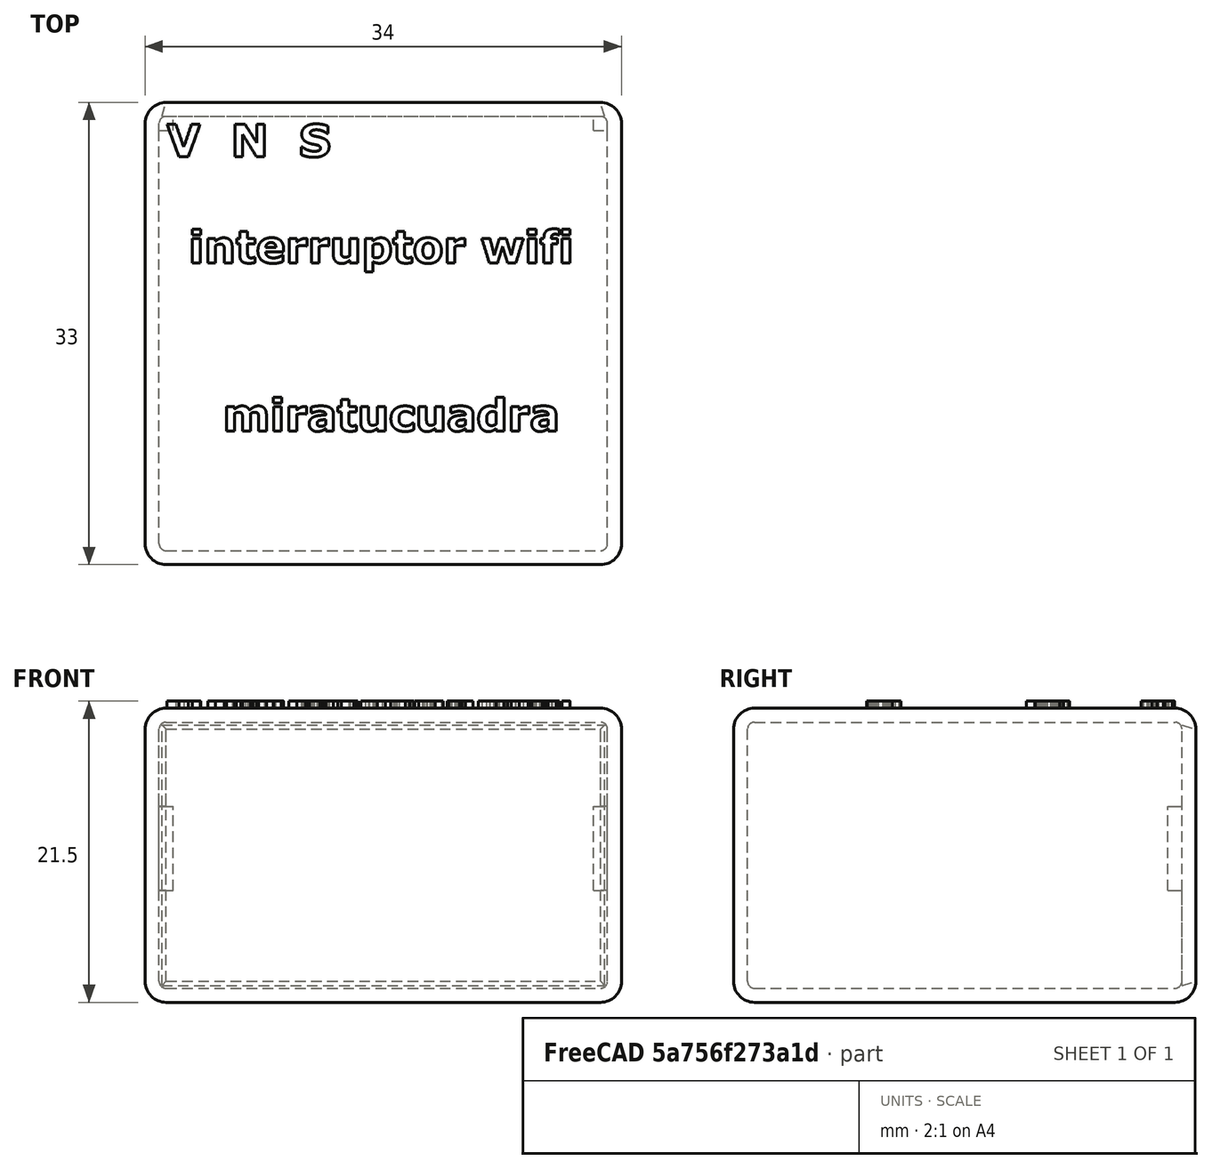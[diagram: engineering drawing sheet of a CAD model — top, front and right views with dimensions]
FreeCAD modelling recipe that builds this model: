
FCSTD DOCUMENT  (FreeCAD 0.20R29410 (Git))
Label: device01_carcaza sola
License: All rights reserved
LicenseURL: http://en.wikipedia.org/wiki/All_rights_reserved
objects: Part::Extrusion×65, Part::Feature×41, Part::Cut×10, Part::Box×5, Part::MultiFuse×5, Part::Fillet×2, Part::Wedge×1
note: 129 computed .brp shape members not serialized (recipe doc carries the construction recipe); baked Part::Feature solids carry a one-line shape summary decoded from their .brp

FEATURE [Part::Box] Box010  label="fundaprisma"
  AttacherType = Attacher::AttachEngine3D
  Height = 21
  Length = 34
  Placement = pos=(-1.3,-7.5,-3) rot=(0,0,1;0rad)
  Width = 33
FEATURE [Part::Feature] path3990
  shape: bbox 2.35 x 2.308 x 2e-07 mm, 0 faces, 0 solids (baked)
FEATURE [Part::Extrusion] Extrude
  Base = -> path3990
  Dir = (0,0,-1)
  DirMode = 2
  FaceMakerClass = Part::FaceMakerBullseye
  LengthFwd = 1
  LengthRev = 0
  Solid = true
  Symmetric = false
FEATURE [Part::Feature] path3992
  shape: bbox 2.099 x 2.308 x 2e-07 mm, 0 faces, 0 solids (baked)
FEATURE [Part::Extrusion] Extrude001
  Base = -> path3992
  Dir = (0,0,-1)
  DirMode = 2
  FaceMakerClass = Part::FaceMakerBullseye
  LengthFwd = 1
  LengthRev = 0
  Solid = true
  Symmetric = false
FEATURE [Part::Feature] path3994
  shape: bbox 1.974 x 2.392 x 2e-07 mm, 0 faces, 0 solids (baked)
FEATURE [Part::Extrusion] Extrude002
  Base = -> path3994
  Dir = (0,0,-1)
  DirMode = 2
  FaceMakerClass = Part::FaceMakerBullseye
  LengthFwd = 1
  LengthRev = 0
  Solid = true
  Symmetric = false
FEATURE [Part::MultiFuse] Fusion003  label="v n s"
  Placement = pos=(6,23,18.5) rot=(0,0,1;0rad)
  Shapes = -> [Extrude002,Extrude,Extrude001]
FEATURE [Part::Feature] path3995
  shape: bbox 0.5581 x 1.741 x 2e-07 mm, 0 faces, 0 solids (baked)
FEATURE [Part::Extrusion] Extrude003
  Base = -> path3995
  Dir = (0,0,-1)
  DirMode = 2
  FaceMakerClass = Part::FaceMakerBullseye
  LengthFwd = 1
  LengthRev = 0
  Solid = true
  Symmetric = false
FEATURE [Part::Extrusion] Extrude022
  Base = -> path3995
  Dir = (0,0,-1)
  DirMode = 2
  FaceMakerClass = Part::FaceMakerBullseye
  LengthFwd = 1
  LengthRev = 0
  Solid = true
  Symmetric = false
FEATURE [Part::Feature] path3990001
  shape: bbox 0.5891 x 0.4232 x 2e-07 mm, 0 faces, 0 solids (baked)
FEATURE [Part::Extrusion] Extrude004
  Base = -> path3990001
  Dir = (0,0,-1)
  DirMode = 2
  FaceMakerClass = Part::FaceMakerBullseye
  LengthFwd = 1
  LengthRev = 0
  Solid = true
  Symmetric = false
FEATURE [Part::Extrusion] Extrude023
  Base = -> path3990001
  Dir = (0,0,-1)
  DirMode = 2
  FaceMakerClass = Part::FaceMakerBullseye
  LengthFwd = 1
  LengthRev = 0
  Solid = true
  Symmetric = false
FEATURE [Part::Feature] path3990002
  shape: bbox 1.749 x 1.789 x 2e-07 mm, 0 faces, 0 solids (baked)
FEATURE [Part::Extrusion] Extrude005
  Base = -> path3990002
  Dir = (0,0,-1)
  DirMode = 2
  FaceMakerClass = Part::FaceMakerBullseye
  LengthFwd = 1
  LengthRev = 0
  Solid = true
  Symmetric = false
FEATURE [Part::Extrusion] Extrude024
  Base = -> path3990002
  Dir = (0,0,-1)
  DirMode = 2
  FaceMakerClass = Part::FaceMakerBullseye
  LengthFwd = 1
  LengthRev = 0
  Solid = true
  Symmetric = false
FEATURE [Part::Feature] path3990003
  shape: bbox 1.31 x 2.273 x 2e-07 mm, 0 faces, 0 solids (baked)
FEATURE [Part::Extrusion] Extrude006
  Base = -> path3990003
  Dir = (0,0,-1)
  DirMode = 2
  FaceMakerClass = Part::FaceMakerBullseye
  LengthFwd = 1
  LengthRev = 0
  Solid = true
  Symmetric = false
FEATURE [Part::Extrusion] Extrude025
  Base = -> path3990003
  Dir = (0,0,-1)
  DirMode = 2
  FaceMakerClass = Part::FaceMakerBullseye
  LengthFwd = 1
  LengthRev = 0
  Solid = true
  Symmetric = false
FEATURE [Part::Feature] path3996
  shape: bbox 1.842 x 1.842 x 2e-07 mm, 0 faces, 0 solids (baked)
FEATURE [Part::Extrusion] Extrude007
  Base = -> path3996
  Dir = (0,0,-1)
  DirMode = 2
  FaceMakerClass = Part::FaceMakerBullseye
  LengthFwd = 1
  LengthRev = 0
  Solid = true
  Symmetric = false
FEATURE [Part::Feature] path3996001
  shape: bbox 0.724 x 0.3519 x 2e-07 mm, 0 faces, 0 solids (baked)
FEATURE [Part::Extrusion] Extrude008
  Base = -> path3996001
  Dir = (0,0,1)
  DirMode = 2
  FaceMakerClass = Part::FaceMakerBullseye
  LengthFwd = 1
  LengthRev = 0
  Placement = pos=(0,0,-1) rot=(0,0,1;0rad)
  Solid = true
  Symmetric = false
FEATURE [Part::Cut] Cut003
  Base = -> Extrude007
  Tool = -> Extrude008
FEATURE [Part::Feature] path3998
  shape: bbox 1.262 x 1.747 x 2e-07 mm, 0 faces, 0 solids (baked)
FEATURE [Part::Extrusion] Extrude009
  Base = -> path3998
  Dir = (0,0,-1)
  DirMode = 2
  FaceMakerClass = Part::FaceMakerBullseye
  LengthFwd = 1
  LengthRev = 0
  Solid = true
  Symmetric = false
FEATURE [Part::Extrusion] Extrude027
  Base = -> path3998
  Dir = (0,0,-1)
  DirMode = 2
  FaceMakerClass = Part::FaceMakerBullseye
  LengthFwd = 1
  LengthRev = 0
  Solid = true
  Symmetric = false
FEATURE [Part::Feature] path4000
  shape: bbox 1.262 x 1.747 x 2e-07 mm, 0 faces, 0 solids (baked)
FEATURE [Part::Extrusion] Extrude010
  Base = -> path4000
  Dir = (0,0,-1)
  DirMode = 2
  FaceMakerClass = Part::FaceMakerBullseye
  LengthFwd = 1
  LengthRev = 0
  Solid = true
  Symmetric = false
FEATURE [Part::Extrusion] Extrude028
  Base = -> path4000
  Dir = (0,0,-1)
  DirMode = 2
  FaceMakerClass = Part::FaceMakerBullseye
  LengthFwd = 1
  LengthRev = 0
  Solid = true
  Symmetric = false
FEATURE [Part::Feature] path4002
  shape: bbox 1.749 x 1.789 x 2e-07 mm, 0 faces, 0 solids (baked)
FEATURE [Part::Extrusion] Extrude011
  Base = -> path4002
  Dir = (0,0,-1)
  DirMode = 2
  FaceMakerClass = Part::FaceMakerBullseye
  LengthFwd = 1
  LengthRev = 0
  Solid = true
  Symmetric = false
FEATURE [Part::Extrusion] Extrude029
  Base = -> path4002
  Dir = (0,0,-1)
  DirMode = 2
  FaceMakerClass = Part::FaceMakerBullseye
  LengthFwd = 1
  LengthRev = 0
  Solid = true
  Symmetric = false
FEATURE [Part::Feature] path4004
  shape: bbox 1.817 x 2.428 x 2e-07 mm, 0 faces, 0 solids (baked)
FEATURE [Part::Extrusion] Extrude030
  Base = -> path4004
  Dir = (0,0,-1)
  DirMode = 2
  FaceMakerClass = Part::FaceMakerBullseye
  LengthFwd = 1
  LengthRev = 0
  Solid = true
  Symmetric = false
FEATURE [Part::Feature] path4004001
  shape: bbox 0.6837 x 1.003 x 2e-07 mm, 0 faces, 0 solids (baked)
FEATURE [Part::Extrusion] Extrude031
  Base = -> path4004001
  Dir = (0,0,1)
  DirMode = 2
  FaceMakerClass = Part::FaceMakerBullseye
  LengthFwd = 1
  LengthRev = 0
  Placement = pos=(0,0,-1) rot=(0,0,1;0rad)
  Solid = true
  Symmetric = false
FEATURE [Part::Cut] Cut004
  Base = -> Extrude030
  Tool = -> Extrude031
FEATURE [Part::Feature] path4006
  shape: bbox 1.31 x 2.273 x 2e-07 mm, 0 faces, 0 solids (baked)
FEATURE [Part::Extrusion] Extrude012
  Base = -> path4006
  Dir = (0,0,-1)
  DirMode = 2
  FaceMakerClass = Part::FaceMakerBullseye
  LengthFwd = 1
  LengthRev = 0
  Solid = true
  Symmetric = false
FEATURE [Part::Extrusion] Extrude032
  Base = -> path4006
  Dir = (0,0,-1)
  DirMode = 2
  FaceMakerClass = Part::FaceMakerBullseye
  LengthFwd = 1
  LengthRev = 0
  Solid = true
  Symmetric = false
FEATURE [Part::Feature] path4008
  shape: bbox 1.907 x 1.849 x 2e-07 mm, 0 faces, 0 solids (baked)
FEATURE [Part::Extrusion] Extrude013
  Base = -> path4008
  Dir = (0,0,-1)
  DirMode = 2
  FaceMakerClass = Part::FaceMakerBullseye
  LengthFwd = 1
  LengthRev = 0
  Solid = true
  Symmetric = false
FEATURE [Part::Feature] path4008001
  shape: bbox 0.7503 x 1.071 x 2e-07 mm, 0 faces, 0 solids (baked)
FEATURE [Part::Extrusion] Extrude014
  Base = -> path4008001
  Dir = (0,0,1)
  DirMode = 2
  FaceMakerClass = Part::FaceMakerBullseye
  LengthFwd = 1
  LengthRev = 0
  Placement = pos=(0,0,-1) rot=(0,0,1;0rad)
  Solid = true
  Symmetric = false
FEATURE [Part::Cut] Cut005
  Base = -> Extrude013
  Tool = -> Extrude014
FEATURE [Part::Feature] path4010
  shape: bbox 1.262 x 1.747 x 2e-07 mm, 0 faces, 0 solids (baked)
FEATURE [Part::Extrusion] Extrude015
  Base = -> path4010
  Dir = (0,0,-1)
  DirMode = 2
  FaceMakerClass = Part::FaceMakerBullseye
  LengthFwd = 1
  LengthRev = 0
  Solid = true
  Symmetric = false
FEATURE [Part::Extrusion] Extrude035
  Base = -> path4010
  Dir = (0,0,-1)
  DirMode = 2
  FaceMakerClass = Part::FaceMakerBullseye
  LengthFwd = 1
  LengthRev = 0
  Solid = true
  Symmetric = false
FEATURE [Part::Feature] path4012
  shape: bbox 2.97 x 1.741 x 2e-07 mm, 0 faces, 0 solids (baked)
FEATURE [Part::Extrusion] Extrude016
  Base = -> path4012
  Dir = (0,0,-1)
  DirMode = 2
  FaceMakerClass = Part::FaceMakerBullseye
  LengthFwd = 1
  LengthRev = 0
  Solid = true
  Symmetric = false
FEATURE [Part::Extrusion] Extrude036
  Base = -> path4012
  Dir = (0,0,-1)
  DirMode = 2
  FaceMakerClass = Part::FaceMakerBullseye
  LengthFwd = 1
  LengthRev = 0
  Solid = true
  Symmetric = false
FEATURE [Part::Feature] path4014
  shape: bbox 0.5581 x 1.741 x 2e-07 mm, 0 faces, 0 solids (baked)
FEATURE [Part::Extrusion] Extrude017
  Base = -> path4014
  Dir = (0,0,-1)
  DirMode = 2
  FaceMakerClass = Part::FaceMakerBullseye
  LengthFwd = 1
  LengthRev = 0
  Solid = true
  Symmetric = false
FEATURE [Part::Extrusion] Extrude037
  Base = -> path4014
  Dir = (0,0,-1)
  DirMode = 2
  FaceMakerClass = Part::FaceMakerBullseye
  LengthFwd = 1
  LengthRev = 0
  Solid = true
  Symmetric = false
FEATURE [Part::Feature] path4014001
  shape: bbox 0.5891 x 0.4232 x 2e-07 mm, 0 faces, 0 solids (baked)
FEATURE [Part::Extrusion] Extrude018
  Base = -> path4014001
  Dir = (0,0,-1)
  DirMode = 2
  FaceMakerClass = Part::FaceMakerBullseye
  LengthFwd = 1
  LengthRev = 0
  Solid = true
  Symmetric = false
FEATURE [Part::Extrusion] Extrude038
  Base = -> path4014001
  Dir = (0,0,-1)
  DirMode = 2
  FaceMakerClass = Part::FaceMakerBullseye
  LengthFwd = 1
  LengthRev = 0
  Solid = true
  Symmetric = false
FEATURE [Part::Feature] path4016
  shape: bbox 1.326 x 2.428 x 2e-07 mm, 0 faces, 0 solids (baked)
FEATURE [Part::Extrusion] Extrude019
  Base = -> path4016
  Dir = (0,0,-1)
  DirMode = 2
  FaceMakerClass = Part::FaceMakerBullseye
  LengthFwd = 1
  LengthRev = 0
  Solid = true
  Symmetric = false
FEATURE [Part::Extrusion] Extrude039
  Base = -> path4016
  Dir = (0,0,-1)
  DirMode = 2
  FaceMakerClass = Part::FaceMakerBullseye
  LengthFwd = 1
  LengthRev = 0
  Solid = true
  Symmetric = false
FEATURE [Part::Feature] path4018
  shape: bbox 0.5581 x 1.741 x 2e-07 mm, 0 faces, 0 solids (baked)
FEATURE [Part::Extrusion] Extrude020
  Base = -> path4018
  Dir = (0,0,-1)
  DirMode = 2
  FaceMakerClass = Part::FaceMakerBullseye
  LengthFwd = 1
  LengthRev = 0
  Solid = true
  Symmetric = false
FEATURE [Part::Extrusion] Extrude040
  Base = -> path4018
  Dir = (0,0,-1)
  DirMode = 2
  FaceMakerClass = Part::FaceMakerBullseye
  LengthFwd = 1
  LengthRev = 0
  Solid = true
  Symmetric = false
FEATURE [Part::Feature] path4018001
  shape: bbox 0.5891 x 0.4232 x 2e-07 mm, 0 faces, 0 solids (baked)
FEATURE [Part::Extrusion] Extrude021
  Base = -> path4018001
  Dir = (0,0,-1)
  DirMode = 2
  FaceMakerClass = Part::FaceMakerBullseye
  LengthFwd = 1
  LengthRev = 0
  Solid = true
  Symmetric = false
FEATURE [Part::Extrusion] Extrude041
  Base = -> path4018001
  Dir = (0,0,-1)
  DirMode = 2
  FaceMakerClass = Part::FaceMakerBullseye
  LengthFwd = 1
  LengthRev = 0
  Solid = true
  Symmetric = false
FEATURE [Part::MultiFuse] Fusion004  label="interruptores"
  Placement = pos=(9,15,18.5) rot=(0,0,1;0rad)
  Shapes = -> [Extrude003,Extrude004,Extrude005,Extrude006,Extrude009,Extrude010,Extrude011,Extrude012,Extrude015,Extrude016,Extrude017,Extrude018,Extrude019,Extrude020,Extrude021,Extrude022,Extrude023,Extrude024,Extrude025,Extrude027,Extrude028,Extrude029,Extrude032,Extrude035,Extrude036,Extrude037,Extrude038,Extrude039,Extrude040,Extrude041,Cut003,Cut004,Cut005]
FEATURE [Part::Feature] path3717
  shape: bbox 2.846 x 1.789 x 2e-07 mm, 0 faces, 0 solids (baked)
FEATURE [Part::Extrusion] Extrude042
  Base = -> path3717
  Dir = (0,0,-1)
  DirMode = 2
  FaceMakerClass = Part::FaceMakerBullseye
  LengthFwd = 1
  LengthRev = 0
  Solid = true
  Symmetric = false
FEATURE [Part::Extrusion] Extrude059
  Base = -> path3717
  Dir = (0,0,-1)
  DirMode = 2
  FaceMakerClass = Part::FaceMakerBullseye
  LengthFwd = 1
  LengthRev = 0
  Solid = true
  Symmetric = false
FEATURE [Part::Feature] path3719
  shape: bbox 0.5581 x 1.741 x 2e-07 mm, 0 faces, 0 solids (baked)
FEATURE [Part::Extrusion] Extrude043
  Base = -> path3719
  Dir = (0,0,-1)
  DirMode = 2
  FaceMakerClass = Part::FaceMakerBullseye
  LengthFwd = 1
  LengthRev = 0
  Solid = true
  Symmetric = false
FEATURE [Part::Extrusion] Extrude060
  Base = -> path3719
  Dir = (0,0,-1)
  DirMode = 2
  FaceMakerClass = Part::FaceMakerBullseye
  LengthFwd = 1
  LengthRev = 0
  Solid = true
  Symmetric = false
FEATURE [Part::Feature] path3719001
  shape: bbox 0.5891 x 0.4232 x 2e-07 mm, 0 faces, 0 solids (baked)
FEATURE [Part::Extrusion] Extrude044
  Base = -> path3719001
  Dir = (0,0,-1)
  DirMode = 2
  FaceMakerClass = Part::FaceMakerBullseye
  LengthFwd = 1
  LengthRev = 0
  Solid = true
  Symmetric = false
FEATURE [Part::Extrusion] Extrude061
  Base = -> path3719001
  Dir = (0,0,-1)
  DirMode = 2
  FaceMakerClass = Part::FaceMakerBullseye
  LengthFwd = 1
  LengthRev = 0
  Solid = true
  Symmetric = false
FEATURE [Part::Feature] path3721
  shape: bbox 1.262 x 1.747 x 2e-07 mm, 0 faces, 0 solids (baked)
FEATURE [Part::Extrusion] Extrude045
  Base = -> path3721
  Dir = (0,0,-1)
  DirMode = 2
  FaceMakerClass = Part::FaceMakerBullseye
  LengthFwd = 1
  LengthRev = 0
  Solid = true
  Symmetric = false
FEATURE [Part::Extrusion] Extrude062
  Base = -> path3721
  Dir = (0,0,-1)
  DirMode = 2
  FaceMakerClass = Part::FaceMakerBullseye
  LengthFwd = 1
  LengthRev = 0
  Solid = true
  Symmetric = false
FEATURE [Part::Feature] path3723
  shape: bbox 0.617 x 0.4868 x 2e-07 mm, 0 faces, 0 solids (baked)
FEATURE [Part::Extrusion] Extrude046
  Base = -> path3723
  Dir = (0,0,1)
  DirMode = 2
  FaceMakerClass = Part::FaceMakerBullseye
  LengthFwd = 1
  LengthRev = 0
  Placement = pos=(0,0,-1) rot=(0,0,1;0rad)
  Solid = true
  Symmetric = false
FEATURE [Part::Feature] path3723001
  shape: bbox 1.738 x 1.837 x 2e-07 mm, 0 faces, 0 solids (baked)
FEATURE [Part::Extrusion] Extrude047
  Base = -> path3723001
  Dir = (0,0,-1)
  DirMode = 2
  FaceMakerClass = Part::FaceMakerBullseye
  LengthFwd = 1
  LengthRev = 0
  Solid = true
  Symmetric = false
FEATURE [Part::Cut] Cut007
  Base = -> Extrude047
  Tool = -> Extrude046
FEATURE [Part::Feature] path3725
  shape: bbox 1.31 x 2.273 x 2e-07 mm, 0 faces, 0 solids (baked)
FEATURE [Part::Extrusion] Extrude048
  Base = -> path3725
  Dir = (0,0,-1)
  DirMode = 2
  FaceMakerClass = Part::FaceMakerBullseye
  LengthFwd = 1
  LengthRev = 0
  Solid = true
  Symmetric = false
FEATURE [Part::Extrusion] Extrude063
  Base = -> path3725
  Dir = (0,0,-1)
  DirMode = 2
  FaceMakerClass = Part::FaceMakerBullseye
  LengthFwd = 1
  LengthRev = 0
  Solid = true
  Symmetric = false
FEATURE [Part::Feature] path3727
  shape: bbox 1.749 x 1.789 x 2e-07 mm, 0 faces, 0 solids (baked)
FEATURE [Part::Extrusion] Extrude049
  Base = -> path3727
  Dir = (0,0,-1)
  DirMode = 2
  FaceMakerClass = Part::FaceMakerBullseye
  LengthFwd = 1
  LengthRev = 0
  Solid = true
  Symmetric = false
FEATURE [Part::Extrusion] Extrude064
  Base = -> path3727
  Dir = (0,0,-1)
  DirMode = 2
  FaceMakerClass = Part::FaceMakerBullseye
  LengthFwd = 1
  LengthRev = 0
  Solid = true
  Symmetric = false
FEATURE [Part::Feature] path3729
  shape: bbox 1.626 x 1.836 x 2e-07 mm, 0 faces, 0 solids (baked)
FEATURE [Part::Extrusion] Extrude050
  Base = -> path3729
  Dir = (0,0,-1)
  DirMode = 2
  FaceMakerClass = Part::FaceMakerBullseye
  LengthFwd = 1
  LengthRev = 0
  Solid = true
  Symmetric = false
FEATURE [Part::Extrusion] Extrude065
  Base = -> path3729
  Dir = (0,0,-1)
  DirMode = 2
  FaceMakerClass = Part::FaceMakerBullseye
  LengthFwd = 1
  LengthRev = 0
  Solid = true
  Symmetric = false
FEATURE [Part::Feature] path3731
  shape: bbox 1.749 x 1.789 x 2e-07 mm, 0 faces, 0 solids (baked)
FEATURE [Part::Extrusion] Extrude051
  Base = -> path3731
  Dir = (0,0,-1)
  DirMode = 2
  FaceMakerClass = Part::FaceMakerBullseye
  LengthFwd = 1
  LengthRev = 0
  Solid = true
  Symmetric = false
FEATURE [Part::Extrusion] Extrude026
  Base = -> path3731
  Dir = (0,0,-1)
  DirMode = 2
  FaceMakerClass = Part::FaceMakerBullseye
  LengthFwd = 1
  LengthRev = 0
  Solid = true
  Symmetric = false
FEATURE [Part::Feature] path3733
  shape: bbox 0.617 x 0.4868 x 2e-07 mm, 0 faces, 0 solids (baked)
FEATURE [Part::Extrusion] Extrude052
  Base = -> path3733
  Dir = (0,0,1)
  DirMode = 2
  FaceMakerClass = Part::FaceMakerBullseye
  LengthFwd = 1
  LengthRev = 0
  Placement = pos=(0,0,-1) rot=(0,0,1;0rad)
  Solid = true
  Symmetric = false
FEATURE [Part::Feature] path3733001
  shape: bbox 1.738 x 1.837 x 2e-07 mm, 0 faces, 0 solids (baked)
FEATURE [Part::Extrusion] Extrude053
  Base = -> path3733001
  Dir = (0,0,-1)
  DirMode = 2
  FaceMakerClass = Part::FaceMakerBullseye
  LengthFwd = 1
  LengthRev = 0
  Solid = true
  Symmetric = false
FEATURE [Part::Cut] Cut008
  Base = -> Extrude053
  Tool = -> Extrude052
FEATURE [Part::Feature] path3735
  shape: bbox 1.817 x 2.46 x 2e-07 mm, 0 faces, 0 solids (baked)
FEATURE [Part::Extrusion] Extrude054
  Base = -> path3735
  Dir = (0,0,-1)
  DirMode = 2
  FaceMakerClass = Part::FaceMakerBullseye
  LengthFwd = 1
  LengthRev = 0
  Solid = true
  Symmetric = false
FEATURE [Part::Feature] path3735001
  shape: bbox 0.6837 x 1.005 x 2e-07 mm, 0 faces, 0 solids (baked)
FEATURE [Part::Extrusion] Extrude055
  Base = -> path3735001
  Dir = (0,0,1)
  DirMode = 2
  FaceMakerClass = Part::FaceMakerBullseye
  LengthFwd = 1
  LengthRev = 0
  Placement = pos=(0,0,-1) rot=(0,0,1;0rad)
  Solid = true
  Symmetric = false
FEATURE [Part::Cut] Cut009
  Base = -> Extrude054
  Tool = -> Extrude055
FEATURE [Part::Feature] path3737
  shape: bbox 1.262 x 1.747 x 2e-07 mm, 0 faces, 0 solids (baked)
FEATURE [Part::Extrusion] Extrude056
  Base = -> path3737
  Dir = (0,0,-1)
  DirMode = 2
  FaceMakerClass = Part::FaceMakerBullseye
  LengthFwd = 1
  LengthRev = 0
  Solid = true
  Symmetric = false
FEATURE [Part::Extrusion] Extrude066
  Base = -> path3737
  Dir = (0,0,-1)
  DirMode = 2
  FaceMakerClass = Part::FaceMakerBullseye
  LengthFwd = 1
  LengthRev = 0
  Solid = true
  Symmetric = false
FEATURE [Part::Feature] path3739
  shape: bbox 0.617 x 0.4868 x 2e-07 mm, 0 faces, 0 solids (baked)
FEATURE [Part::Extrusion] Extrude057
  Base = -> path3739
  Dir = (0,0,1)
  DirMode = 2
  FaceMakerClass = Part::FaceMakerBullseye
  LengthFwd = 1
  LengthRev = 0
  Placement = pos=(0,0,-1) rot=(0,0,1;0rad)
  Solid = true
  Symmetric = false
FEATURE [Part::Feature] path3739001
  shape: bbox 1.738 x 1.837 x 2e-07 mm, 0 faces, 0 solids (baked)
FEATURE [Part::Extrusion] Extrude058
  Base = -> path3739001
  Dir = (0,0,-1)
  DirMode = 2
  FaceMakerClass = Part::FaceMakerBullseye
  LengthFwd = 1
  LengthRev = 0
  Solid = true
  Symmetric = false
FEATURE [Part::Cut] Cut010
  Base = -> Extrude058
  Tool = -> Extrude057
FEATURE [Part::MultiFuse] Fusion005  label="miratucuadra"
  Placement = pos=(15,3,18.5) rot=(0,0,1;0rad)
  Shapes = -> [Extrude042,Extrude043,Extrude044,Extrude045,Extrude048,Extrude049,Extrude050,Extrude051,Extrude056,Extrude059,Extrude060,Extrude061,Extrude062,Extrude063,Extrude064,Extrude065,Extrude026,Extrude066,Cut007,Cut008,Cut009,Cut010]
FEATURE [Part::Box] Box019  label="prisma int"
  AttacherType = Attacher::AttachEngine3D
  Height = 19
  Length = 32
  Placement = pos=(-0.3,-6.5,-2) rot=(0,0,1;0rad)
  Width = 31
FEATURE [Part::Fillet] Fillet  label="externo"
  Base = -> Box010
  Edges = 12 edges r=1.5: [Edge1,Edge2,Edge3,Edge4,Edge5,Edge6,Edge7,Edge8,Edge9,Edge10,Edge11,Edge12]
FEATURE [Part::Fillet] Fillet001  label="interno"
  Base = -> Box019
  Edges = 12 edges r=0.5: [Edge1,Edge2,Edge3,Edge4,Edge5,Edge6,Edge7,Edge8,Edge9,Edge10,Edge11,Edge12]
FEATURE [Part::Cut] Cut
  Base = -> Fillet
  Tool = -> Fillet001
FEATURE [Part::Box] Box020  label="Cubo"
  AttacherType = Attacher::AttachEngine3D
  Height = 18
  Length = 31
  Placement = pos=(0.2,23,-1.5) rot=(0,0,1;0rad)
  Width = 3
FEATURE [Part::Cut] Cut011
  Base = -> Cut
  Tool = -> Box020
FEATURE [Part::Wedge] Wedge001  label="Cuña001"
  AttacherType = Attacher::AttachEngine3D
  Placement = pos=(-0.1,24.5,-1.8) rot=(0,0,1;0rad)
  X2max = 31.3
  X2min = 0.3
  Xmax = 31.6
  Xmin = 0
  Ymax = 1
  Ymin = 0
  Z2max = 18.3
  Z2min = 0.3
  Zmax = 18.6
  Zmin = 0
FEATURE [Part::Cut] Cut012  label="carcasa sin texto"
  Base = -> Cut011
  Tool = -> Wedge001
FEATURE [Part::Box] Box028  label="Cubo008"
  AttacherType = Attacher::AttachEngine3D
  Height = 6
  Length = 1
  Placement = pos=(-0.3,23.5,5) rot=(0,0,1;0rad)
  Width = 1
FEATURE [Part::Box] Box029  label="Cubo009"
  AttacherType = Attacher::AttachEngine3D
  Height = 6
  Length = 1
  Placement = pos=(30.7,23.5,5) rot=(0,0,1;0rad)
  Width = 1
FEATURE [Part::MultiFuse] Fusion008
  Shapes = -> [Box029,Box028,Cut012]
FEATURE [Part::MultiFuse] Fusion009  label="carcaza"
  Shapes = -> [Fusion008,Fusion003,Fusion004,Fusion005]
